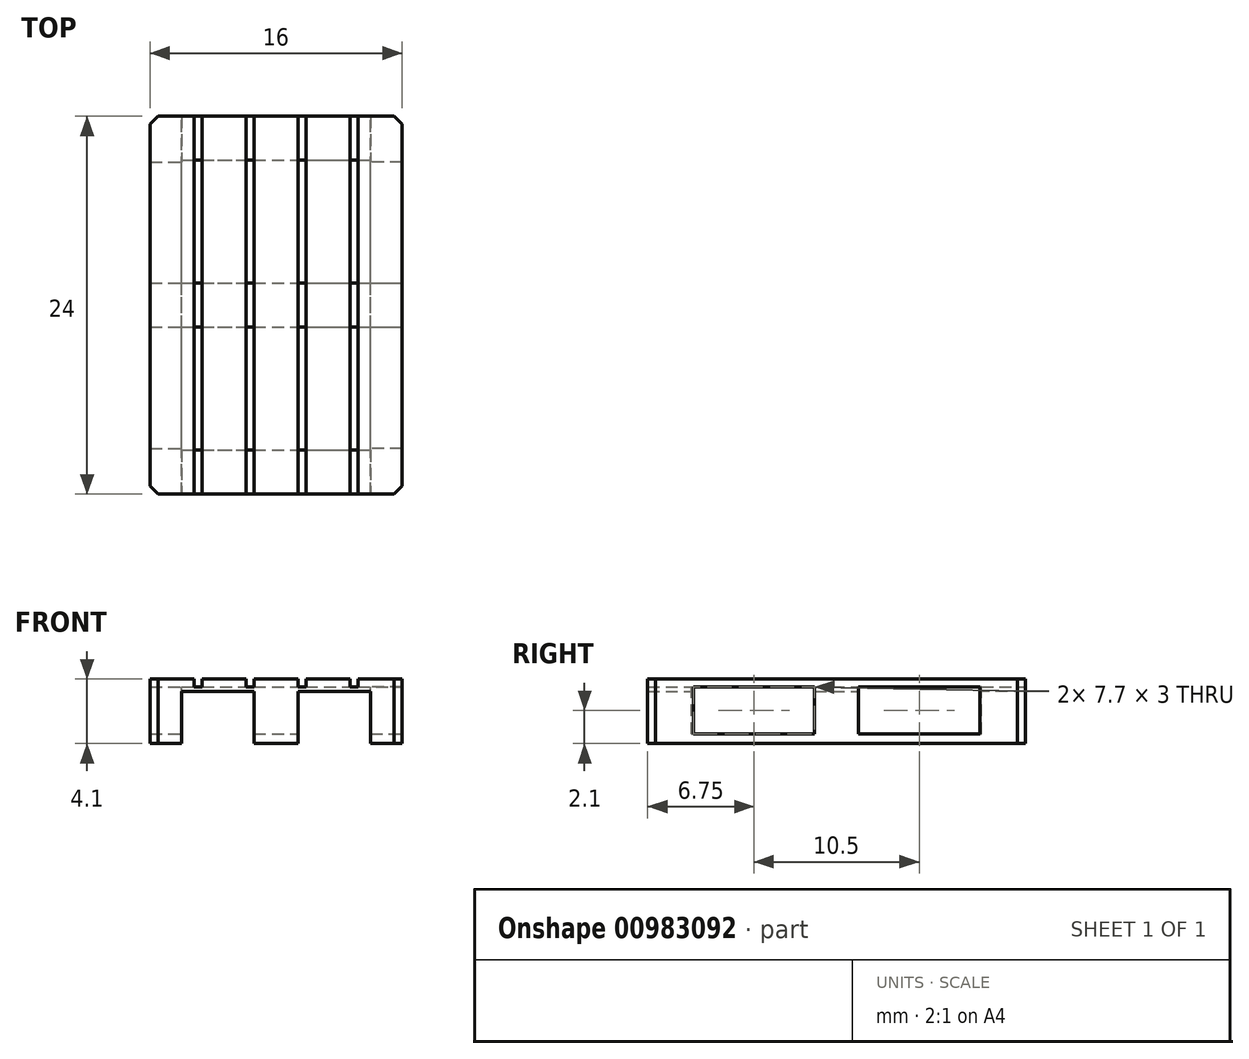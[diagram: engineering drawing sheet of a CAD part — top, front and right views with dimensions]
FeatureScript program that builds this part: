
annotation { "Feature Type Name" : "Feature", "Feature Type Description" : "" }
export const myFeature = defineFeature(function(context is Context, id is Id, definition is map)
    precondition{}
    {
        {
            var Q0;
            Q0=qCreatedBy(makeId("Top.planeOp"),FACE);
            var sketch = newSketch(context, id + "F0", { "sketchPlane" : qUnion([Q0])});
            skLineSegment(sketch, "E0.bottom", {"start": v(0, 0) * mm, "end": v(2.8, 0) * mm});
            skLineSegment(sketch, "E0.top", {"start": v(0, 24) * mm, "end": v(2.8, 24) * mm});
            skLineSegment(sketch, "E0.left", {"start": v(0, 0) * mm, "end": v(0, 24) * mm});
            skLineSegment(sketch, "E0.right", {"start": v(2.8, 0) * mm, "end": v(2.8, 24) * mm});
            skLineSegment(sketch, "E1", {"start": v(2.8, 0) * mm, "end": v(3.3, 0) * mm, "construction": true});
            skLineSegment(sketch, "E2.bottom", {"start": v(3.3, 0) * mm, "end": v(6.1, 0) * mm});
            skLineSegment(sketch, "E2.top", {"start": v(3.3, 24) * mm, "end": v(6.1, 24) * mm});
            skLineSegment(sketch, "E2.left", {"start": v(3.3, 0) * mm, "end": v(3.3, 24) * mm});
            skLineSegment(sketch, "E2.right", {"start": v(6.1, 0) * mm, "end": v(6.1, 24) * mm});
            skLineSegment(sketch, "E3.bottom", {"start": v(6.6, 0) * mm, "end": v(9.4, 0) * mm});
            skLineSegment(sketch, "E3.top", {"start": v(6.6, 24) * mm, "end": v(9.4, 24) * mm});
            skLineSegment(sketch, "E3.left", {"start": v(6.6, 0) * mm, "end": v(6.6, 24) * mm});
            skLineSegment(sketch, "E3.right", {"start": v(9.4, 0) * mm, "end": v(9.4, 24) * mm});
            skLineSegment(sketch, "E4.bottom", {"start": v(9.9, 0) * mm, "end": v(12.7, 0) * mm});
            skLineSegment(sketch, "E4.top", {"start": v(9.9, 24) * mm, "end": v(12.7, 24) * mm});
            skLineSegment(sketch, "E4.left", {"start": v(9.9, 0) * mm, "end": v(9.9, 24) * mm});
            skLineSegment(sketch, "E4.right", {"start": v(12.7, 0) * mm, "end": v(12.7, 24) * mm});
            skLineSegment(sketch, "E5.bottom", {"start": v(13.2, 0) * mm, "end": v(16, 0) * mm});
            skLineSegment(sketch, "E5.top", {"start": v(13.2, 24) * mm, "end": v(16, 24) * mm});
            skLineSegment(sketch, "E5.left", {"start": v(13.2, 0) * mm, "end": v(13.2, 24) * mm});
            skLineSegment(sketch, "E5.right", {"start": v(16, 0) * mm, "end": v(16, 24) * mm});
            skSolve(sketch);
        }
        {
            var Q0;
            Q0 = qSketchRegion(id + "F0", true);
            extrude(context, id + "F1", {"entities" : qUnion([Q0]), "depth" : 0.5 * mm, "offsetDistance" : 25 * mm});
        }
        {
            var Q0;
            Q0=makeQuery(id+"F1.opExtrude","CAP_FACE",FACE,{"disambiguationData":[OSD([sQuery(id+"F0.wireOp",EDGE,"E0.bottom"),sQuery(id+"F0.wireOp",EDGE,"E0.top"),sQuery(id+"F0.wireOp",EDGE,"E0.left"),sQuery(id+"F0.wireOp",EDGE,"E0.right")])],"isStart":true});
            var sketch = newSketch(context, id + "F2", { "sketchPlane" : qUnion([Q0])});
            skLineSegment(sketch, "E6.bottom", {"start": v(0, 0) * mm, "end": v(2, 0) * mm});
            skLineSegment(sketch, "E6.top", {"start": v(0, -2.9) * mm, "end": v(2, -2.9) * mm});
            skLineSegment(sketch, "E6.left", {"start": v(0, 0) * mm, "end": v(0, -2.9) * mm});
            skLineSegment(sketch, "E6.right", {"start": v(2, 0) * mm, "end": v(2, -2.9) * mm});
            skLineSegment(sketch, "E7.bottom", {"start": v(0, -24) * mm, "end": v(2, -24) * mm});
            skLineSegment(sketch, "E7.top", {"start": v(0, -21.1) * mm, "end": v(2, -21.1) * mm});
            skLineSegment(sketch, "E7.left", {"start": v(0, -24) * mm, "end": v(0, -21.1) * mm});
            skLineSegment(sketch, "E7.right", {"start": v(2, -24) * mm, "end": v(2, -21.1) * mm});
            skPoint(sketch, "E8.0", {"position": v(16, 0) * mm});
            skPoint(sketch, "E9.0", {"position": v(16, -24) * mm});
            skLineSegment(sketch, "E10.bottom", {"start": v(16, 0) * mm, "end": v(14, 0) * mm});
            skLineSegment(sketch, "E10.top", {"start": v(16, -2.9) * mm, "end": v(14, -2.9) * mm});
            skLineSegment(sketch, "E10.left", {"start": v(16, 0) * mm, "end": v(16, -2.9) * mm});
            skLineSegment(sketch, "E10.right", {"start": v(14, 0) * mm, "end": v(14, -2.9) * mm});
            skLineSegment(sketch, "E11.bottom", {"start": v(16, -24) * mm, "end": v(14, -24) * mm});
            skLineSegment(sketch, "E11.top", {"start": v(16, -21.1) * mm, "end": v(14, -21.1) * mm});
            skLineSegment(sketch, "E11.left", {"start": v(16, -24) * mm, "end": v(16, -21.1) * mm});
            skLineSegment(sketch, "E11.right", {"start": v(14, -24) * mm, "end": v(14, -21.1) * mm});
            skSolve(sketch);
        }
        {
            var Q0;
            {var subQ1=sQuery(id+"F2.wireOp",EDGE,"E6.top");Q0=makeQuery(id+"F2.imprint","IMPRINT",FACE,{"disambiguationData":[TD([[makeQuery(id+"F2.imprint","IMPRINT",EDGE,{"derivedFrom":subQ1}),-1.0]])]});}
            var sketch = newSketch(context, id + "F3", { "sketchPlane" : qUnion([Q0])});
            skLineSegment(sketch, "E12.bottom", {"start": v(0, 0) * mm, "end": v(16, 0) * mm});
            skLineSegment(sketch, "E12.top", {"start": v(0, -2.8) * mm, "end": v(16, -2.8) * mm});
            skLineSegment(sketch, "E12.left", {"start": v(0, 0) * mm, "end": v(0, -2.8) * mm});
            skLineSegment(sketch, "E12.right", {"start": v(16, 0) * mm, "end": v(16, -2.8) * mm});
            skPoint(sketch, "E13.0", {"position": v(0, -24) * mm});
            skLineSegment(sketch, "E14.bottom", {"start": v(0, -24) * mm, "end": v(16, -24) * mm});
            skLineSegment(sketch, "E14.top", {"start": v(0, -21.2) * mm, "end": v(16, -21.2) * mm});
            skLineSegment(sketch, "E14.left", {"start": v(0, -24) * mm, "end": v(0, -21.2) * mm});
            skLineSegment(sketch, "E14.right", {"start": v(16, -24) * mm, "end": v(16, -21.2) * mm});
            skPoint(sketch, "E15.0", {"position": v(0, -12) * mm});
            skLineSegment(sketch, "E16.bottom", {"start": v(0, -10.6) * mm, "end": v(16, -10.6) * mm});
            skLineSegment(sketch, "E16.top", {"start": v(0, -13.4) * mm, "end": v(16, -13.4) * mm});
            skLineSegment(sketch, "E16.left", {"start": v(0, -10.6) * mm, "end": v(0, -13.4) * mm});
            skLineSegment(sketch, "E16.right", {"start": v(16, -10.6) * mm, "end": v(16, -13.4) * mm});
            skSolve(sketch);
        }
        {
            var Q0;
            Q0 = qSketchRegion(id + "F3", true);
            extrude(context, id + "F4", {"entities" : qUnion([Q0]), "depth" : 0.3 * mm, "offsetDistance" : 25 * mm});
        }
        {
            var Q0;
            Q0 = qSketchRegion(id + "F2", true);
            extrude(context, id + "F5", {"entities" : qUnion([Q0]), "depth" : 3 * mm, "offsetDistance" : 25 * mm});
        }
        {
            var Q0;
            Q0=makeQuery(id+"F4.opExtrude","CAP_FACE",FACE,{"disambiguationData":[OSD([sQuery(id+"F3.wireOp",EDGE,"E16.bottom"),sQuery(id+"F3.wireOp",EDGE,"E16.top"),sQuery(id+"F3.wireOp",EDGE,"E16.left"),sQuery(id+"F3.wireOp",EDGE,"E16.right")])],"isStart":false});
            var sketch = newSketch(context, id + "F6", { "sketchPlane" : qUnion([Q0])});
            skLineSegment(sketch, "E17.bottom", {"start": v(0, -10.6) * mm, "end": v(2, -10.6) * mm});
            skLineSegment(sketch, "E17.top", {"start": v(0, -13.4) * mm, "end": v(2, -13.4) * mm});
            skLineSegment(sketch, "E17.left", {"start": v(0, -10.6) * mm, "end": v(0, -13.4) * mm});
            skLineSegment(sketch, "E17.right", {"start": v(2, -10.6) * mm, "end": v(2, -13.4) * mm});
            skLineSegment(sketch, "E18.bottom", {"start": v(16, -10.6) * mm, "end": v(14, -10.6) * mm});
            skLineSegment(sketch, "E18.top", {"start": v(16, -13.4) * mm, "end": v(14, -13.4) * mm});
            skLineSegment(sketch, "E18.left", {"start": v(16, -10.6) * mm, "end": v(16, -13.4) * mm});
            skLineSegment(sketch, "E18.right", {"start": v(14, -10.6) * mm, "end": v(14, -13.4) * mm});
            skSolve(sketch);
        }
        {
            var Q0;
            Q0 = qSketchRegion(id + "F6", true);
            extrude(context, id + "F7", {"entities" : qUnion([Q0]), "operationType" : NewBodyOperationType.ADD, "depth" : 2.7 * mm, "offsetDistance" : 25 * mm});
        }
        {
            var Q0;
            Q0=makeQuery(id+"F5.opExtrude","CAP_FACE",FACE,{"disambiguationData":[OSD([sQuery(id+"F2.wireOp",EDGE,"E6.bottom"),sQuery(id+"F2.wireOp",EDGE,"E6.top"),sQuery(id+"F2.wireOp",EDGE,"E6.left"),sQuery(id+"F2.wireOp",EDGE,"E6.right")])],"isStart":false});
            var sketch = newSketch(context, id + "F8", { "sketchPlane" : qUnion([Q0])});
            skPoint(sketch, "E19.0", {"position": v(2, -24) * mm});
            skLineSegment(sketch, "E20.bottom", {"start": v(0, 0) * mm, "end": v(2, 0) * mm});
            skLineSegment(sketch, "E20.top", {"start": v(0, -24) * mm, "end": v(2, -24) * mm});
            skLineSegment(sketch, "E20.left", {"start": v(0, 0) * mm, "end": v(0, -24) * mm});
            skLineSegment(sketch, "E20.right", {"start": v(2, 0) * mm, "end": v(2, -24) * mm});
            skPoint(sketch, "E21.0", {"position": v(16, 0) * mm});
            skPoint(sketch, "E22.0", {"position": v(16, -24) * mm});
            skPoint(sketch, "E23.0", {"position": v(14, -24) * mm});
            skLineSegment(sketch, "E24.bottom", {"start": v(16, 0) * mm, "end": v(14, 0) * mm});
            skLineSegment(sketch, "E24.top", {"start": v(16, -24) * mm, "end": v(14, -24) * mm});
            skLineSegment(sketch, "E24.left", {"start": v(16, 0) * mm, "end": v(16, -24) * mm});
            skLineSegment(sketch, "E24.right", {"start": v(14, 0) * mm, "end": v(14, -24) * mm});
            skSolve(sketch);
        }
        {
            var Q0;
            Q0=makeQuery(id+"F4.opExtrude","CAP_FACE",FACE,{"disambiguationData":[OSD([sQuery(id+"F3.wireOp",EDGE,"E12.bottom"),sQuery(id+"F3.wireOp",EDGE,"E12.top"),sQuery(id+"F3.wireOp",EDGE,"E12.left"),sQuery(id+"F3.wireOp",EDGE,"E12.right")])],"isStart":false});
            var sketch = newSketch(context, id + "F9", { "sketchPlane" : qUnion([Q0])});
            skLineSegment(sketch, "E25.bottom", {"start": v(6.6, 0) * mm, "end": v(9.4, 0) * mm});
            skLineSegment(sketch, "E25.top", {"start": v(6.6, -2.8) * mm, "end": v(9.4, -2.8) * mm});
            skLineSegment(sketch, "E25.left", {"start": v(6.6, 0) * mm, "end": v(6.6, -2.8) * mm});
            skLineSegment(sketch, "E25.right", {"start": v(9.4, 0) * mm, "end": v(9.4, -2.8) * mm});
            skPoint(sketch, "E26", {"position": v(8, 0) * mm});
            skLineSegment(sketch, "E27.bottom", {"start": v(6.6, -21.2) * mm, "end": v(9.4, -21.2) * mm});
            skLineSegment(sketch, "E27.top", {"start": v(6.6, -24) * mm, "end": v(9.4, -24) * mm});
            skLineSegment(sketch, "E27.left", {"start": v(6.6, -21.2) * mm, "end": v(6.6, -24) * mm});
            skLineSegment(sketch, "E27.right", {"start": v(9.4, -21.2) * mm, "end": v(9.4, -24) * mm});
            skPoint(sketch, "E28", {"position": v(8, -24) * mm});
            skLineSegment(sketch, "E29.bottom", {"start": v(6.6, -10.6) * mm, "end": v(9.4, -10.6) * mm});
            skLineSegment(sketch, "E29.top", {"start": v(6.6, -13.4) * mm, "end": v(9.4, -13.4) * mm});
            skLineSegment(sketch, "E29.left", {"start": v(6.6, -10.6) * mm, "end": v(6.6, -13.4) * mm});
            skLineSegment(sketch, "E29.right", {"start": v(9.4, -10.6) * mm, "end": v(9.4, -13.4) * mm});
            skPoint(sketch, "E30", {"position": v(8, -10.6) * mm});
            skSolve(sketch);
        }
        {
            var Q0;
            Q0 = qSketchRegion(id + "F9", true);
            extrude(context, id + "F10", {"entities" : qUnion([Q0]), "depth" : 2.7 * mm, "offsetDistance" : 25 * mm});
        }
        {
            var Q0;
            {var subQ0=sQuery(id+"F8.wireOp",EDGE,"E20.bottom");Q0=makeQuery(id+"F8.imprint","IMPRINT",FACE,{"disambiguationData":[TD([[makeQuery(id+"F8.imprint","IMPRINT",EDGE,{"derivedFrom":subQ0}),-1.0]])]});}
            var sketch = newSketch(context, id + "F11", { "sketchPlane" : qUnion([Q0])});
            skPoint(sketch, "E31.0", {"position": v(2, -24) * mm});
            skLineSegment(sketch, "E32.bottom", {"start": v(0, 0) * mm, "end": v(2, 0) * mm});
            skLineSegment(sketch, "E32.top", {"start": v(0, -24) * mm, "end": v(2, -24) * mm});
            skLineSegment(sketch, "E32.left", {"start": v(0, 0) * mm, "end": v(0, -24) * mm});
            skLineSegment(sketch, "E32.right", {"start": v(2, 0) * mm, "end": v(2, -24) * mm});
            skPoint(sketch, "E33.0", {"position": v(6.6, 0) * mm});
            skPoint(sketch, "E34.0", {"position": v(9.4, -24) * mm});
            skLineSegment(sketch, "E35.bottom", {"start": v(6.6, 0) * mm, "end": v(9.4, 0) * mm});
            skLineSegment(sketch, "E35.top", {"start": v(6.6, -24) * mm, "end": v(9.4, -24) * mm});
            skLineSegment(sketch, "E35.left", {"start": v(6.6, 0) * mm, "end": v(6.6, -24) * mm});
            skLineSegment(sketch, "E35.right", {"start": v(9.4, 0) * mm, "end": v(9.4, -24) * mm});
            skPoint(sketch, "E36.0", {"position": v(14, 0) * mm});
            skPoint(sketch, "E37.0", {"position": v(16, -24) * mm});
            skLineSegment(sketch, "E38.bottom", {"start": v(14, 0) * mm, "end": v(16, 0) * mm});
            skLineSegment(sketch, "E38.top", {"start": v(14, -24) * mm, "end": v(16, -24) * mm});
            skLineSegment(sketch, "E38.left", {"start": v(14, 0) * mm, "end": v(14, -24) * mm});
            skLineSegment(sketch, "E38.right", {"start": v(16, 0) * mm, "end": v(16, -24) * mm});
            skSolve(sketch);
        }
        {
            var Q0;
            Q0 = qSketchRegion(id + "F11", true);
            extrude(context, id + "F12", {"entities" : qUnion([Q0]), "depth" : 0.6 * mm, "offsetDistance" : 25 * mm});
        }
        {
            var Q0;
            Q0=makeQuery(id+"F1.opExtrude","SWEPT_BODY",BODY,{"disambiguationData":[OSD([sQuery(id+"F0.wireOp",EDGE,"E0.bottom"),sQuery(id+"F0.wireOp",EDGE,"E0.top"),sQuery(id+"F0.wireOp",EDGE,"E0.left"),sQuery(id+"F0.wireOp",EDGE,"E0.right")])]});
            var Q1;
            Q1=makeQuery(id+"F1.opExtrude","SWEPT_BODY",BODY,{"disambiguationData":[OSD([sQuery(id+"F0.wireOp",EDGE,"E2.bottom"),sQuery(id+"F0.wireOp",EDGE,"E2.top"),sQuery(id+"F0.wireOp",EDGE,"E2.left"),sQuery(id+"F0.wireOp",EDGE,"E2.right")])]});
            var Q2;
            Q2=makeQuery(id+"F1.opExtrude","SWEPT_BODY",BODY,{"disambiguationData":[OSD([sQuery(id+"F0.wireOp",EDGE,"E3.bottom"),sQuery(id+"F0.wireOp",EDGE,"E3.top"),sQuery(id+"F0.wireOp",EDGE,"E3.left"),sQuery(id+"F0.wireOp",EDGE,"E3.right")])]});
            var Q3;
            Q3=makeQuery(id+"F1.opExtrude","SWEPT_BODY",BODY,{"disambiguationData":[OSD([sQuery(id+"F0.wireOp",EDGE,"E4.bottom"),sQuery(id+"F0.wireOp",EDGE,"E4.top"),sQuery(id+"F0.wireOp",EDGE,"E4.left"),sQuery(id+"F0.wireOp",EDGE,"E4.right")])]});
            var Q4;
            Q4=makeQuery(id+"F1.opExtrude","SWEPT_BODY",BODY,{"disambiguationData":[OSD([sQuery(id+"F0.wireOp",EDGE,"E5.bottom"),sQuery(id+"F0.wireOp",EDGE,"E5.top"),sQuery(id+"F0.wireOp",EDGE,"E5.left"),sQuery(id+"F0.wireOp",EDGE,"E5.right")])]});
            var Q5;
            Q5=makeQuery(id+"F4.opExtrude","SWEPT_BODY",BODY,{"disambiguationData":[OSD([sQuery(id+"F3.wireOp",EDGE,"E12.bottom"),sQuery(id+"F3.wireOp",EDGE,"E12.top"),sQuery(id+"F3.wireOp",EDGE,"E12.left"),sQuery(id+"F3.wireOp",EDGE,"E12.right")])]});
            var Q6;
            Q6=makeQuery(id+"F4.opExtrude","SWEPT_BODY",BODY,{"disambiguationData":[OSD([sQuery(id+"F3.wireOp",EDGE,"E14.bottom"),sQuery(id+"F3.wireOp",EDGE,"E14.top"),sQuery(id+"F3.wireOp",EDGE,"E14.left"),sQuery(id+"F3.wireOp",EDGE,"E14.right")])]});
            var Q7;
            Q7=makeQuery(id+"F4.opExtrude","SWEPT_BODY",BODY,{"disambiguationData":[OSD([sQuery(id+"F3.wireOp",EDGE,"E16.bottom"),sQuery(id+"F3.wireOp",EDGE,"E16.top"),sQuery(id+"F3.wireOp",EDGE,"E16.left"),sQuery(id+"F3.wireOp",EDGE,"E16.right")])]});
            var Q8;
            Q8=makeQuery(id+"F5.opExtrude","SWEPT_BODY",BODY,{"disambiguationData":[OSD([sQuery(id+"F2.wireOp",EDGE,"E6.bottom"),sQuery(id+"F2.wireOp",EDGE,"E6.top"),sQuery(id+"F2.wireOp",EDGE,"E6.left"),sQuery(id+"F2.wireOp",EDGE,"E6.right")])]});
            var Q9;
            Q9=makeQuery(id+"F5.opExtrude","SWEPT_BODY",BODY,{"disambiguationData":[OSD([sQuery(id+"F2.wireOp",EDGE,"E7.bottom"),sQuery(id+"F2.wireOp",EDGE,"E7.top"),sQuery(id+"F2.wireOp",EDGE,"E7.left"),sQuery(id+"F2.wireOp",EDGE,"E7.right")])]});
            var Q10;
            Q10=makeQuery(id+"F5.opExtrude","SWEPT_BODY",BODY,{"disambiguationData":[OSD([sQuery(id+"F2.wireOp",EDGE,"E10.bottom"),sQuery(id+"F2.wireOp",EDGE,"E10.top"),sQuery(id+"F2.wireOp",EDGE,"E10.left"),sQuery(id+"F2.wireOp",EDGE,"E10.right")])]});
            var Q11;
            Q11=makeQuery(id+"F5.opExtrude","SWEPT_BODY",BODY,{"disambiguationData":[OSD([sQuery(id+"F2.wireOp",EDGE,"E11.bottom"),sQuery(id+"F2.wireOp",EDGE,"E11.top"),sQuery(id+"F2.wireOp",EDGE,"E11.left"),sQuery(id+"F2.wireOp",EDGE,"E11.right")])]});
            var Q12;
            Q12=makeQuery(id+"F10.opExtrude","SWEPT_BODY",BODY,{"disambiguationData":[OSD([sQuery(id+"F9.wireOp",EDGE,"E25.bottom"),sQuery(id+"F9.wireOp",EDGE,"E25.top"),sQuery(id+"F9.wireOp",EDGE,"E25.left"),sQuery(id+"F9.wireOp",EDGE,"E25.right")])]});
            var Q13;
            Q13=makeQuery(id+"F10.opExtrude","SWEPT_BODY",BODY,{"disambiguationData":[OSD([sQuery(id+"F9.wireOp",EDGE,"E27.bottom"),sQuery(id+"F9.wireOp",EDGE,"E27.top"),sQuery(id+"F9.wireOp",EDGE,"E27.left"),sQuery(id+"F9.wireOp",EDGE,"E27.right")])]});
            var Q14;
            Q14=makeQuery(id+"F10.opExtrude","SWEPT_BODY",BODY,{"disambiguationData":[OSD([sQuery(id+"F9.wireOp",EDGE,"E29.bottom"),sQuery(id+"F9.wireOp",EDGE,"E29.top"),sQuery(id+"F9.wireOp",EDGE,"E29.left"),sQuery(id+"F9.wireOp",EDGE,"E29.right")])]});
            var Q15;
            Q15=makeQuery(id+"F12.opExtrude","SWEPT_BODY",BODY,{"disambiguationData":[OSD([sQuery(id+"F11.wireOp",EDGE,"E32.bottom"),sQuery(id+"F11.wireOp",EDGE,"E32.top"),sQuery(id+"F11.wireOp",EDGE,"E32.left"),sQuery(id+"F11.wireOp",EDGE,"E32.right")])]});
            var Q16;
            Q16=makeQuery(id+"F12.opExtrude","SWEPT_BODY",BODY,{"disambiguationData":[OSD([sQuery(id+"F11.wireOp",EDGE,"E35.bottom"),sQuery(id+"F11.wireOp",EDGE,"E35.top"),sQuery(id+"F11.wireOp",EDGE,"E35.left"),sQuery(id+"F11.wireOp",EDGE,"E35.right")])]});
            var Q17;
            Q17=makeQuery(id+"F12.opExtrude","SWEPT_BODY",BODY,{"disambiguationData":[OSD([sQuery(id+"F11.wireOp",EDGE,"E38.bottom"),sQuery(id+"F11.wireOp",EDGE,"E38.top"),sQuery(id+"F11.wireOp",EDGE,"E38.left"),sQuery(id+"F11.wireOp",EDGE,"E38.right")])]});
            booleanBodies(context, id + "F13", {"operationType" : BooleanOperationType.UNION, "tools" : qUnion([Q0, Q1, Q2, Q3, Q4, Q5, Q6, Q7, Q8, Q9, Q10, Q11, Q12, Q13, Q14, Q15, Q16, Q17])});
        }
        {
            var Q0;
            Q0=makeQuery(id+"F13.opBoolean","MERGE",EDGE,{"derivedFrom":[makeQuery(id+"F1.opExtrude","SWEPT_EDGE",EDGE,{"disambiguationData":[OSD([sQuery(id+"F0.wireOp",EDGE,"E0.top"),sQuery(id+"F0.wireOp",EDGE,"E0.left")])]}),makeQuery(id+"F4.opExtrude","SWEPT_EDGE",EDGE,{"disambiguationData":[OSD([sQuery(id+"F3.wireOp",EDGE,"E14.bottom"),sQuery(id+"F3.wireOp",EDGE,"E14.left")])]}),makeQuery(id+"F5.opExtrude","SWEPT_EDGE",EDGE,{"disambiguationData":[OSD([sQuery(id+"F2.wireOp",EDGE,"E7.bottom"),sQuery(id+"F2.wireOp",EDGE,"E7.left")])]}),makeQuery(id+"F12.opExtrude","SWEPT_EDGE",EDGE,{"disambiguationData":[OSD([sQuery(id+"F11.wireOp",EDGE,"E32.top"),sQuery(id+"F11.wireOp",EDGE,"E32.left")])]})]});
            var Q1;
            Q1=makeQuery(id+"F13.opBoolean","MERGE",EDGE,{"derivedFrom":[makeQuery(id+"F1.opExtrude","SWEPT_EDGE",EDGE,{"disambiguationData":[OSD([sQuery(id+"F0.wireOp",EDGE,"E5.top"),sQuery(id+"F0.wireOp",EDGE,"E5.right")])]}),makeQuery(id+"F4.opExtrude","SWEPT_EDGE",EDGE,{"disambiguationData":[OSD([sQuery(id+"F3.wireOp",EDGE,"E14.bottom"),sQuery(id+"F3.wireOp",EDGE,"E14.right")])]}),makeQuery(id+"F5.opExtrude","SWEPT_EDGE",EDGE,{"disambiguationData":[OSD([sQuery(id+"F2.wireOp",EDGE,"E11.bottom"),sQuery(id+"F2.wireOp",EDGE,"E11.left")])]}),makeQuery(id+"F12.opExtrude","SWEPT_EDGE",EDGE,{"disambiguationData":[OSD([sQuery(id+"F11.wireOp",EDGE,"E38.top"),sQuery(id+"F11.wireOp",EDGE,"E38.right")])]})]});
            var Q2;
            Q2=makeQuery(id+"F13.opBoolean","MERGE",EDGE,{"derivedFrom":[makeQuery(id+"F1.opExtrude","SWEPT_EDGE",EDGE,{"disambiguationData":[OSD([sQuery(id+"F0.wireOp",EDGE,"E0.bottom"),sQuery(id+"F0.wireOp",EDGE,"E0.left")])]}),makeQuery(id+"F4.opExtrude","SWEPT_EDGE",EDGE,{"disambiguationData":[OSD([sQuery(id+"F3.wireOp",EDGE,"E12.bottom"),sQuery(id+"F3.wireOp",EDGE,"E12.left")])]}),makeQuery(id+"F5.opExtrude","SWEPT_EDGE",EDGE,{"disambiguationData":[OSD([sQuery(id+"F2.wireOp",EDGE,"E6.bottom"),sQuery(id+"F2.wireOp",EDGE,"E6.left")])]}),makeQuery(id+"F12.opExtrude","SWEPT_EDGE",EDGE,{"disambiguationData":[OSD([sQuery(id+"F11.wireOp",EDGE,"E32.bottom"),sQuery(id+"F11.wireOp",EDGE,"E32.left")])]})]});
            var Q3;
            Q3=makeQuery(id+"F13.opBoolean","MERGE",EDGE,{"derivedFrom":[makeQuery(id+"F1.opExtrude","SWEPT_EDGE",EDGE,{"disambiguationData":[OSD([sQuery(id+"F0.wireOp",EDGE,"E5.bottom"),sQuery(id+"F0.wireOp",EDGE,"E5.right")])]}),makeQuery(id+"F4.opExtrude","SWEPT_EDGE",EDGE,{"disambiguationData":[OSD([sQuery(id+"F3.wireOp",EDGE,"E12.bottom"),sQuery(id+"F3.wireOp",EDGE,"E12.right")])]}),makeQuery(id+"F5.opExtrude","SWEPT_EDGE",EDGE,{"disambiguationData":[OSD([sQuery(id+"F2.wireOp",EDGE,"E10.bottom"),sQuery(id+"F2.wireOp",EDGE,"E10.left")])]}),makeQuery(id+"F12.opExtrude","SWEPT_EDGE",EDGE,{"disambiguationData":[OSD([sQuery(id+"F11.wireOp",EDGE,"E38.bottom"),sQuery(id+"F11.wireOp",EDGE,"E38.right")])]})]});
            chamfer(context, id + "F14", {"entities" : qUnion([Q0, Q1, Q2, Q3]), "width" : 0.5 * mm, "tangentPropagation" : true});
        }
    });
